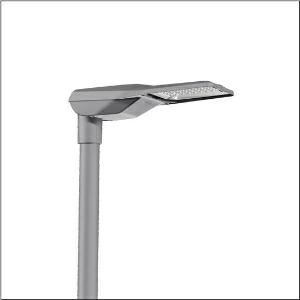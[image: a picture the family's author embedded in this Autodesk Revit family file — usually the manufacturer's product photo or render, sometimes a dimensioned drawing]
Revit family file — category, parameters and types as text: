
# Revit family: streetlight_sl_21_iq_mini___stw1_0a_5xe2e31g08hb_9864
name_source: partatom
category: Lighting Fixtures
units: mm (PartAtom-declared; Revit-internal decimal feet)

## family parameters
Cut with Voids When Loaded = No
Host = Face
Light Source = No
Part Type = Normal
Room Calculation Point = No
Round Connector Dimension = Use Diameter
Shared = No

## types (1)
- --- (1 x LED, 9450 lm, 70.9 W, 3000K)
    Apparent Load = 71 VA
    CIE Flux Codes = 38 75 98 100 100
    Color Rendering = 70
    Color Temperature = 3000K
    Default Elevation = 1800 mm
    Description = Streetlight SL 21 iQ mini, mast luminaire, primary light control with lens, of PMMA, primary optical cover: cover, of toughened safety glass, transparent, light distribution: STW1.0a, light emission: direct distribution, primary light characteristic: asymmetric, installation type: post-top, side-entry, LED, High Power LED, rated luminous flux: 9.450lm, luminous efficacy: 133lm/W, light colour: 730, colour temperature: 3000K, control: Street-Remote, Auto-Match, Temp-Guard, Lumen-Switch, Night-Set, Smart-Wire, Light-Fading, Desk-Remote (wireless, voltage-free reading and setting of iQ features in the workshop via application-optimized NFC function/RFID function), optimised constant luminous flux control (CLO 2.0), pre-setting: linear dimming characteristic, mains connection: 220..240V, AC, 50/60Hz, start of lifetime: 71W, end of service life: 75W, reduction: 31W, luminaire housing, of diecast aluminium, powder-coated, Siteco® metallic grey (DB 702S), corrosivity category C5 mid according to DIN EN ISO 12944, please order mast flange separately, inclination adjustable: 0°, 5°, 10°, 15°, sealing non-destructively replaceable, multi-level sealing system, length: 628mm, width: 235mm, height: 110mm, mast flange for spigot size: 42mm (side-entry): 5XC10008XM4, 60/48mm (side-entry/post-top): 5XC10108XM2, 76/60mm (side-entry/post-top): 5XC10108XM1, protection rating (complete): IP66, insulation class (complete): insulation class II (safety insulation), certification: CE, ENEC, ENEC+, VDE, impact resistance: IK09, permissible operating ambient temperature for outdoor applications: -40..+50°C, standard-compliant lighting for roads and squares, packaging unit: 1 piece

Light Distribution: STW1.0a
    Height = 110 mm
    Lamp = 1 x LED
    Lamp Light Flux = 9450 lm
    Lamp Power = 70.9 W
    Lamp count = 1
    Length = 625 mm
    Luminous efficacy = 133 lm/W
    Manufacturer = Siteco
    ModVariant = No
    Model = 5XE2E31G08HB
    Number of Poles = 1
    OnlyDefault = Yes
    Power Factor = 1
    Product Name = Streetlight SL 21 iQ mini | STW1.0a
    Product group = mast luminaire | pylon top
    ProductGroupID = 6100
    Protection Class = Protection class II
    Protection Degree = IP 66
    RLX_Detail_Level = 1
    RLX_Emergency_Light_Flux = 0 lm
    RLX_Emergency_Type = 0
    RLX_Emergency_Type_DB = No
    RlxData = <blob elided: 92213 chars, md5=2aba2a36>
    Socket = socket
    Standby Power = 0 W
    System Light Flux = 9450 lm
    System Power = 71 W
    Type Comments = factory setting: luminous flux: 100 % | dim-lin: 254 | 711 mA
    Type Image = l_1003519.jpg
    URL = http://relux.com
    VarID = @adj_128179
    Voltage = 0 V
    Weight = 0.00 kg
    Width = 234 mm

## geometry (parser evidence)
native form markers: Blend x4, Sweep x12
no freeform markers — native parametric forms only
